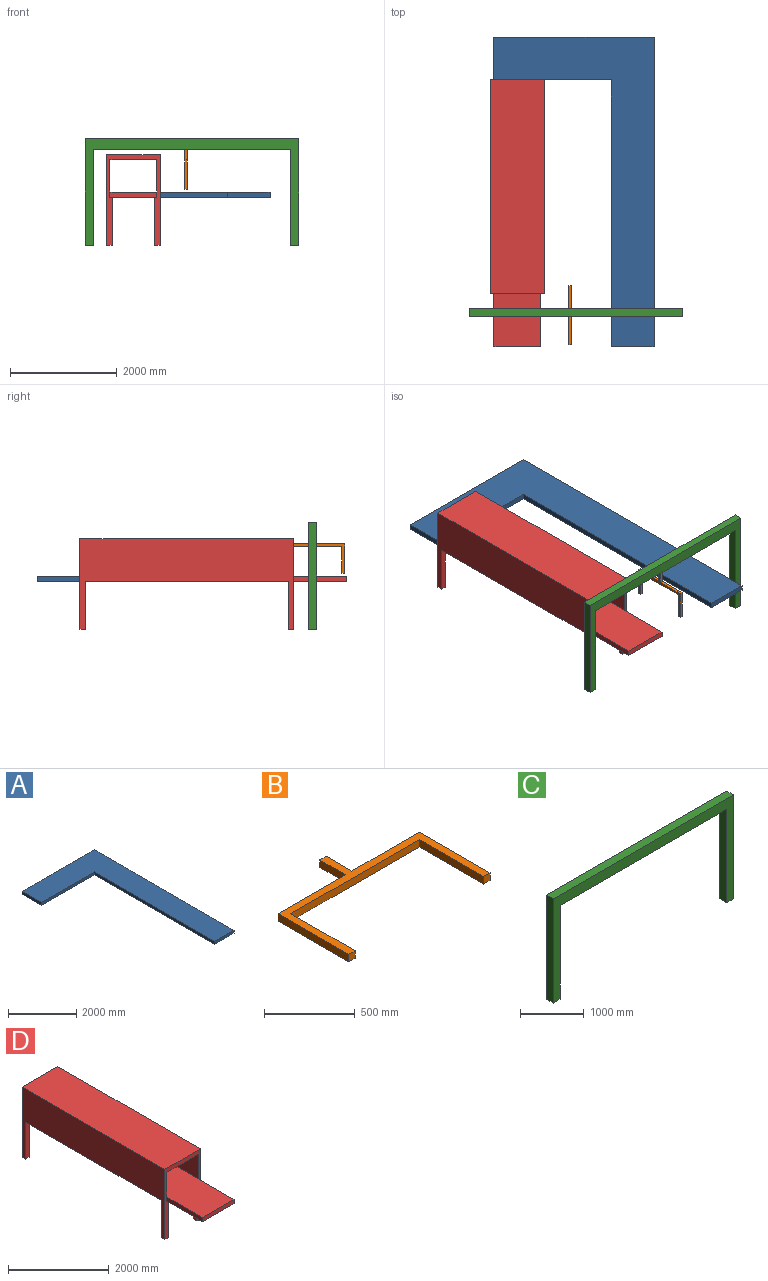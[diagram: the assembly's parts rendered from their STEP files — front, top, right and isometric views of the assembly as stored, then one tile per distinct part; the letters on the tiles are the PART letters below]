
ASSEMBLY  parts=4 mates=5
PART A: 8 faces, bbox 3000x5800x100 mm
  f0: plane 2200x100mm, normal (0,-1,0), area 220000mm2, adj f1,f5,f6,f7
  f1: plane 5000x100mm, normal (-1,0,0), area 500000mm2, adj f0,f2,f6,f7
  f2: plane 800x100mm, normal (0,-1,0), area 80000mm2, adj f1,f3,f6,f7
  f3: plane 5800x100mm, normal (1,0,0), area 580000mm2, adj f2,f4,f6,f7
  f4: plane 3000x100mm, normal (0,1,0), area 300000mm2, adj f3,f5,f6,f7
  f5: plane 800x100mm, normal (-1,0,0), area 80000mm2, adj f0,f4,f6,f7
  f6: plane 5800x3000mm, normal (0,0,1), area 6400000mm2, adj f0,f1,f2,f3,f4,f5
  f7: plane 5800x3000mm, normal (0,0,-1), area 6400000mm2, adj f0,f1,f2,f3,f4,f5
PART B: 14 faces, bbox 1100x750x50 mm
  f0: plane 525x50mm, normal (0,1,0), area 26250mm2, adj f1,f11,f12,f13
  f1: plane 200x50mm, normal (1,0,0), area 10000mm2, adj f0,f2,f12,f13
  f2: plane 50x50mm, normal (0,1,0), area 2500mm2, adj f1,f3,f12,f13
  f3: plane 200x50mm, normal (-1,0,0), area 10000mm2, adj f2,f4,f12,f13
  f4: plane 525x50mm, normal (0,1,0), area 26250mm2, adj f3,f5,f12,f13
  f5: plane 550x50mm, normal (-1,0,0), area 27500mm2, adj f4,f6,f12,f13
  f6: plane 50x50mm, normal (0,-1,0), area 2500mm2, adj f5,f7,f12,f13
  f7: plane 500x50mm, normal (1,0,0), area 25000mm2, adj f6,f8,f12,f13
  f8: plane 1000x50mm, normal (0,-1,0), area 50000mm2, adj f7,f9,f12,f13
  f9: plane 500x50mm, normal (-1,0,0), area 25000mm2, adj f8,f10,f12,f13
  f10: plane 50x50mm, normal (0,-1,0), area 2500mm2, adj f9,f11,f12,f13
  f11: plane 550x50mm, normal (1,0,0), area 27500mm2, adj f0,f10,f12,f13
  f12: plane 1100x750mm, normal (0,0,1), area 115000mm2, adj f0,f1,f2,f3,f4,f5,f6,f7
  f13: plane 1100x750mm, normal (0,0,-1), area 115000mm2, adj f0,f1,f2,f3,f4,f5,f6,f7
PART C: 10 faces, bbox 4000x150x2000 mm
  f0: plane 2000x150mm, normal (-1,0,0), area 300000mm2, adj f1,f7,f8,f9
  f1: plane 150x150mm, normal (0,0,-1), area 22500mm2, adj f0,f2,f8,f9
  f2: plane 1800x150mm, normal (1,0,0), area 270000mm2, adj f1,f3,f8,f9
  f3: plane 3700x150mm, normal (0,0,-1), area 555000mm2, adj f2,f4,f8,f9
  f4: plane 1800x150mm, normal (-1,0,0), area 270000mm2, adj f3,f5,f8,f9
  f5: plane 150x150mm, normal (0,0,-1), area 22500mm2, adj f4,f6,f8,f9
  f6: plane 2000x150mm, normal (1,0,0), area 300000mm2, adj f5,f7,f8,f9
  f7: plane 4000x150mm, normal (0,0,1), area 600000mm2, adj f0,f6,f8,f9
  f8: plane 4000x2000mm, normal (0,-1,0), area 1340000mm2, adj f0,f1,f2,f3,f4,f5,f6,f7
  f9: plane 4000x2000mm, normal (0,1,0), area 1340000mm2, adj f0,f1,f2,f3,f4,f5,f6,f7
PART D: 25 faces, bbox 1000x5000x1700 mm
  f0: plane 5000x880mm, normal (0,0,1), area 4400000mm2, adj f1,f7,f9,f22,f23,f24
  f1: plane 4000x600mm, normal (1,0,0), area 2400000mm2, adj f0,f2,f8,f9
  f2: plane 4000x880mm, normal (0,0,-1), area 3520000mm2, adj f1,f7,f8,f9
  f3: plane 4000x1700mm, normal (-1,0,0), area 3380000mm2, adj f4,f6,f8,f9,f10,f12,f14,f15
  f4: plane 5000x1000mm, normal (0,0,-1), area 4840000mm2, adj f3,f5,f8,f9,f10,f11,f13,f14
  f5: plane 4000x1700mm, normal (1,0,0), area 3380000mm2, adj f4,f6,f8,f9,f17,f18,f19,f21
  f6: plane 4000x1000mm, normal (0,0,1), area 4000000mm2, adj f3,f5,f8,f9
  f7: plane 4000x600mm, normal (-1,0,0), area 2400000mm2, adj f0,f2,f8,f9
  f8: plane 1700x1000mm, normal (0,-1,0), area 364000mm2, adj f1,f2,f3,f4,f5,f6,f7,f11
  f9: plane 1700x1000mm, normal (0,1,0), area 452000mm2, adj f0,f1,f2,f3,f4,f5,f6,f7
  f10: plane 900x100mm, normal (0,1,0), area 90000mm2, adj f3,f4,f11,f12
  f11: plane 900x100mm, normal (1,0,0), area 90000mm2, adj f4,f8,f10,f12
  f12: plane 100x100mm, normal (0,0,-1), area 10000mm2, adj f3,f8,f10,f11
  f13: plane 900x100mm, normal (1,0,0), area 90000mm2, adj f4,f9,f14,f15
  f14: plane 900x100mm, normal (0,-1,0), area 90000mm2, adj f3,f4,f13,f15
  f15: plane 100x100mm, normal (0,0,-1), area 10000mm2, adj f3,f9,f13,f14
  f16: plane 900x100mm, normal (-1,0,0), area 90000mm2, adj f4,f8,f17,f18
  f17: plane 900x100mm, normal (0,1,0), area 90000mm2, adj f4,f5,f16,f18
  f18: plane 100x100mm, normal (0,0,-1), area 10000mm2, adj f5,f8,f16,f17
  f19: plane 900x100mm, normal (0,-1,0), area 90000mm2, adj f4,f5,f20,f21
  f20: plane 900x100mm, normal (-1,0,0), area 90000mm2, adj f4,f9,f19,f21
  f21: plane 100x100mm, normal (0,0,-1), area 10000mm2, adj f5,f9,f19,f20
  f22: plane 1000x100mm, normal (-1,0,0), area 100000mm2, adj f0,f4,f8,f24
  f23: plane 1000x100mm, normal (1,0,0), area 100000mm2, adj f0,f4,f8,f24
  f24: plane 880x100mm, normal (0,-1,0), area 88000mm2, adj f0,f4,f22,f23
PLACE A t=(-2262.3,1114.87,300.47)mm
PLACE B rot(axis=(0.58,-0.58,-0.58),120deg) t=(-811.56,-3295.09,450.47)mm
PLACE C t=(-724.73,-3170.09,-599.53)mm
PLACE D t=(-1822.3,-885.13,300.47)mm fixed
MATE planar C.f8 <-> B.f1  axis (0,-1,0) through (-724.73,-3320.09,897.48)mm
MATE fastened A.f6 <-> D.f0  axis (0,0,1) through (-2262.3,1114.87,400.47)mm
MATE planar B.f2 <-> C.f3  axis (0,0,1) through (-836.56,-3295.09,1200.47)mm
MATE parallel B.f12 <-> D.f5  axis (-1,0,0) through (-861.56,-3270.09,1000.47)mm
MATE planar C.f1 <-> D.f12  axis (0,0,-1) through (-2649.73,-3245.09,-599.53)mm
